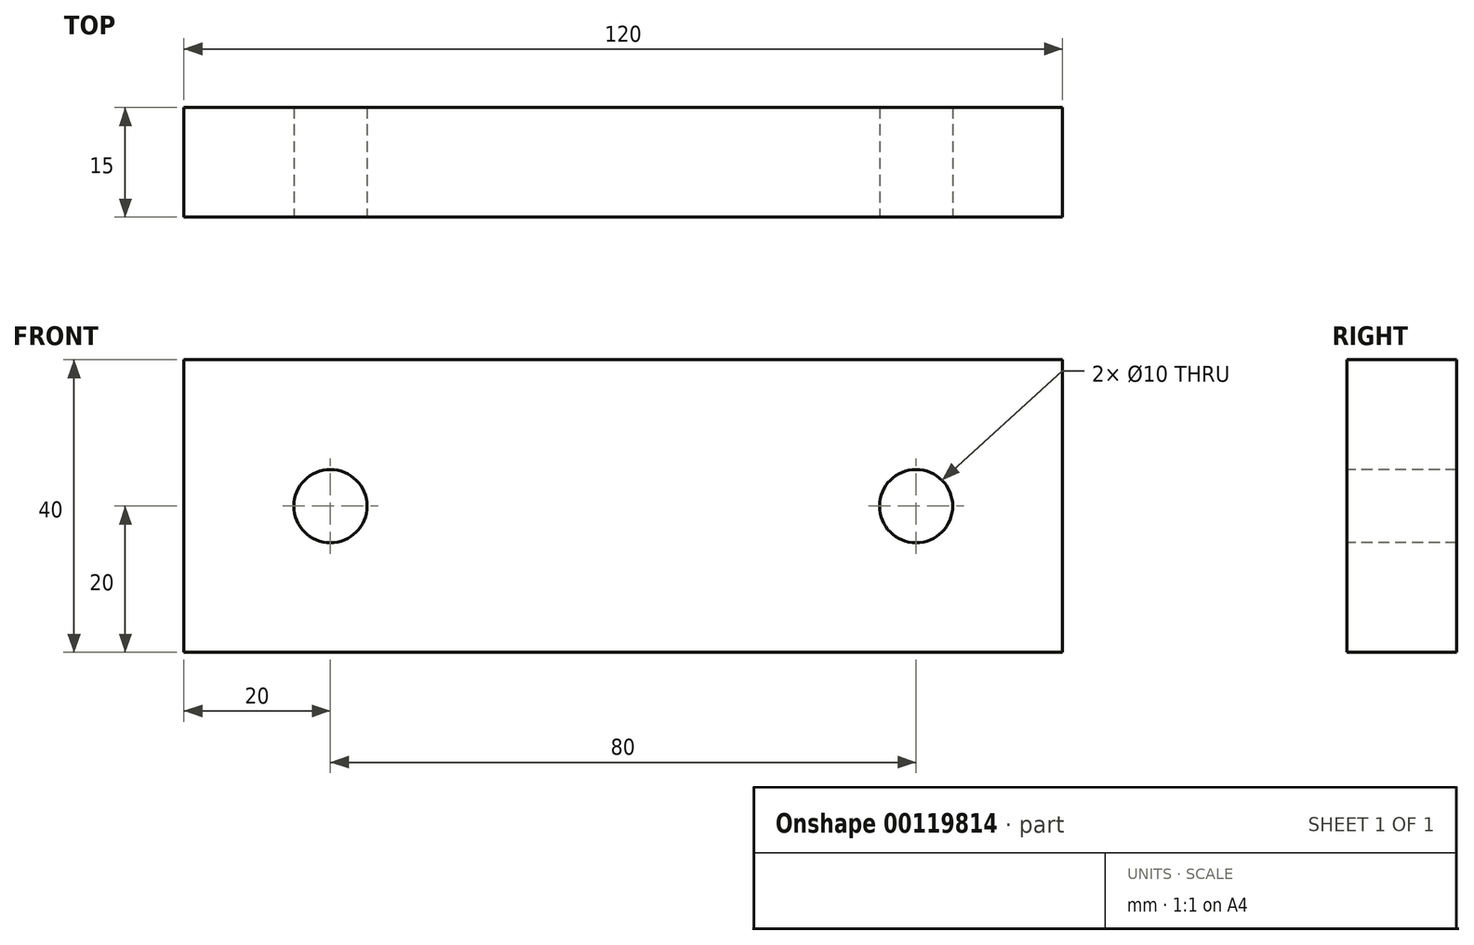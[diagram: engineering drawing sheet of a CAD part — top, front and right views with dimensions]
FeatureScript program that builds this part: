
annotation { "Feature Type Name" : "Feature", "Feature Type Description" : "" }
export const myFeature = defineFeature(function(context is Context, id is Id, definition is map)
    precondition{}
    {
        {
            var Q0;
            Q0=qCreatedBy(makeId("Front.planeOp"),FACE);
            var sketch = newSketch(context, id + "F0", { "sketchPlane" : qUnion([Q0])});
            skLineSegment(sketch, "E0.bottom", {"start": v(0, 0) * mm, "end": v(120, 0) * mm});
            skLineSegment(sketch, "E0.top", {"start": v(0, 40) * mm, "end": v(120, 40) * mm});
            skLineSegment(sketch, "E0.left", {"start": v(0, 0) * mm, "end": v(0, 40) * mm});
            skLineSegment(sketch, "E0.right", {"start": v(120, 0) * mm, "end": v(120, 40) * mm});
            skSolve(sketch);
        }
        {
            var Q0;
            Q0 = qSketchRegion(id + "F0", true);
            extrude(context, id + "F1", {"entities" : qUnion([Q0]), "depth" : 15 * mm});
        }
        {
            var Q0;
            Q0=makeQuery(id+"F1.opExtrude","CAP_FACE",FACE,{"disambiguationData":[OSD([sQuery(id+"F0.wireOp",EDGE,"E0.bottom"),sQuery(id+"F0.wireOp",EDGE,"E0.top"),sQuery(id+"F0.wireOp",EDGE,"E0.left"),sQuery(id+"F0.wireOp",EDGE,"E0.right")])],"isStart":false});
            var sketch = newSketch(context, id + "F2", { "sketchPlane" : qUnion([Q0])});
            skCircle(sketch, "E1", {"center": v(20, 20) * mm, "radius": 5 * mm});
            skCircle(sketch, "E2", {"center": v(100, 20) * mm, "radius": 5 * mm});
            skSolve(sketch);
        }
        {
            var Q0;
            Q0=makeQuery(id+"F2.imprint","IMPRINT",FACE,{"disambiguationData":[TD([[makeQuery(id+"F2.imprint","IMPRINT",EDGE,{"derivedFrom":sQuery(id+"F2.wireOp",EDGE,"E2")}),1.0]])]});
            var Q1;
            Q1=makeQuery(id+"F2.imprint","IMPRINT",FACE,{"disambiguationData":[TD([[makeQuery(id+"F2.imprint","IMPRINT",EDGE,{"derivedFrom":sQuery(id+"F2.wireOp",EDGE,"E1")}),1.0]])]});
            extrude(context, id + "F3", {"entities" : qUnion([Q0, Q1]), "operationType" : NewBodyOperationType.REMOVE, "oppositeDirection" : true, "depth" : 15 * mm});
        }
    });
